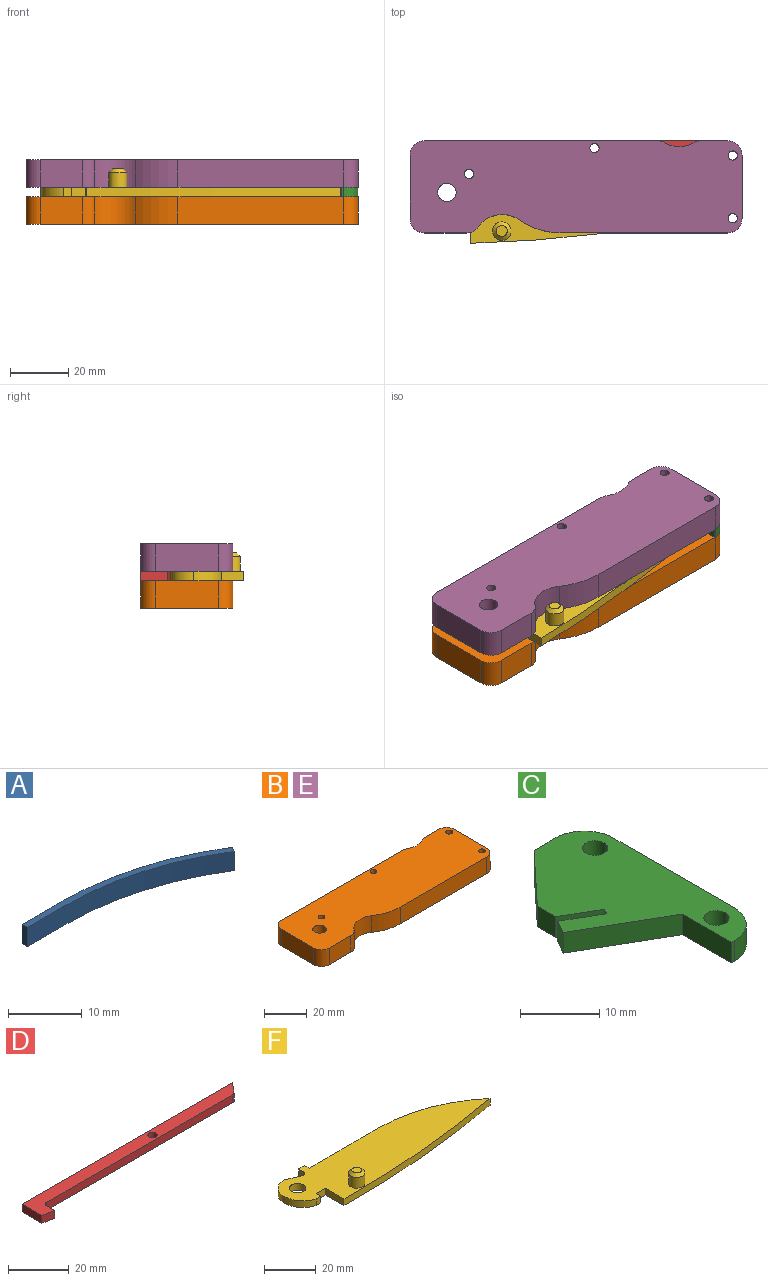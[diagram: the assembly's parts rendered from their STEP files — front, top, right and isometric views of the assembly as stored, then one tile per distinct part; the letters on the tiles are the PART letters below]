
ASSEMBLY  parts=6 mates=5
PART A: 8 faces, bbox 33x8.2x3.2 mm
  f0: plane 7.62x3.18mm, normal (0,1,0), area 24.2mm2, adj f1,f5,f6,f7
  f1: plane 3.18x1.02mm, normal (-1,0,0), area 3.2mm2, adj f0,f2,f6,f7
  f2: plane 7.62x3.18mm, normal (0,-1,0), area 24.2mm2, adj f1,f3,f6,f7
  f3: cylinder r=46.46mm len=24.86mm, axis (0,0,-1), area 83.3mm2, adj f2,f4,f6,f7
  f4: plane 3.18x0.86mm, normal (0.84,-0.54,0), area 3.2mm2, adj f3,f5,f6,f7
  f5: cylinder r=47.48mm len=25.4mm, axis (0,0,-1), area 85.1mm2, adj f0,f4,f6,f7
  f6: plane 33.02x8.22mm, normal (0,0,1), area 34.7mm2, adj f0,f1,f2,f3,f4,f5
  f7: plane 33.02x8.22mm, normal (0,0,-1), area 34.7mm2, adj f0,f1,f2,f3,f4,f5
PART B: 23 faces, bbox 114.3x31.8x9.5 mm
  f0: plane 80.03x9.53mm, normal (0,1,0), area 762.3mm2, adj f11,f12,f15,f20
  f1: plane 14.29x9.53mm, normal (0,-1,0), area 136.1mm2, adj f11,f12,f16,f19
  f2: plane 9.53x8.91mm, normal (0,1,0), area 84.8mm2, adj f11,f12,f18,f21
  f3: plane 21.59x9.53mm, normal (-1,0,0), area 205.6mm2, adj f11,f12,f15,f16
  f4: plane 57.19x9.53mm, normal (0,-1,0), area 544.7mm2, adj f11,f12,f17,f22
  f5: cylinder r=1.59mm len=9.53mm, axis (0,0,-1), area 95mm2, adj f11,f12
  f6: cylinder r=1.59mm len=9.53mm, axis (0,0,-1), area 95mm2, adj f11,f12
  f7: cylinder r=1.59mm len=9.53mm, axis (0,0,-1), area 95mm2, adj f11,f12
  f8: cylinder r=3.17mm len=9.53mm, axis (0,0,-1), area 190mm2, adj f11,f12
  f9: plane 21.59x9.53mm, normal (1,0,0), area 205.6mm2, adj f11,f12,f17,f18
  f10: cylinder r=1.59mm len=9.53mm, axis (0,0,-1), area 95mm2, adj f11,f12
  f11: plane 114.3x31.75mm, normal (0,0,1), area 3427.2mm2, adj f0,f1,f2,f3,f4,f5,f6,f7
  f12: plane 114.3x31.75mm, normal (0,0,-1), area 3427.2mm2, adj f0,f1,f2,f3,f4,f5,f6,f7
  f13: cylinder r=10.16mm len=10.14mm, axis (0,0,1), area 101.1mm2, adj f11,f12,f20,f21
  f14: cylinder r=10.16mm len=14.05mm, axis (0,0,1), area 150.5mm2, adj f11,f12,f19,f22
  f15: cylinder r=5.08mm len=9.53mm, axis (0,0,1), area 76mm2, adj f0,f3,f11,f12
  f16: cylinder r=5.08mm len=9.53mm, axis (0,0,-1), area 76mm2, adj f1,f3,f11,f12
  f17: cylinder r=5.08mm len=9.53mm, axis (0,0,1), area 76mm2, adj f4,f9,f11,f12
  f18: cylinder r=5.08mm len=9.53mm, axis (0,0,-1), area 76mm2, adj f2,f9,f11,f12
  f19: cylinder r=5.08mm len=9.53mm, axis (0,0,1), area 45.9mm2, adj f1,f11,f12,f14
  f20: cylinder r=5.08mm len=9.53mm, axis (0,0,1), area 25.3mm2, adj f0,f11,f12,f13
  f21: cylinder r=5.08mm len=9.53mm, axis (0,0,1), area 25.3mm2, adj f2,f11,f12,f13
  f22: cylinder r=25.4mm len=14.49mm, axis (0,0,1), area 146.8mm2, adj f4,f11,f12,f14
PART C: 17 faces, bbox 19.1x31.8x3.2 mm
  f0: plane 3.18x0.51mm, normal (0,-1,0), area 1.6mm2, adj f1,f6,f9,f15
  f1: plane 31.75x19.05mm, normal (0,0,1), area 340.3mm2, adj f0,f2,f3,f4,f5,f7,f8,f9
  f2: plane 21.59x3.18mm, normal (1,0,0), area 68.5mm2, adj f1,f6,f15,f16
  f3: plane 3.9x3.18mm, normal (0,1,0), area 12.4mm2, adj f1,f6,f8,f16
  f4: cylinder r=1.59mm len=3.18mm, axis (0,0,-1), area 31.7mm2, adj f1,f6
  f5: cylinder r=1.59mm len=3.18mm, axis (0,0,-1), area 31.7mm2, adj f1,f6
  f6: plane 31.75x19.05mm, normal (0,0,-1), area 340.3mm2, adj f0,f2,f3,f4,f5,f7,f8,f9
  f7: plane 3.27x3.18mm, normal (-1,0,0), area 10.4mm2, adj f1,f6,f8,f14
  f8: plane 8.89x8.29mm, normal (-0.73,0.68,0), area 38.6mm2, adj f1,f3,f6,f7
  f9: plane 8.74x3.18mm, normal (-1,0,0), area 27.7mm2, adj f0,f1,f6,f10
  f10: plane 13.46x7.77mm, normal (-0.5,-0.87,0), area 49.4mm2, adj f1,f6,f9,f11
  f11: plane 3.18x2.2mm, normal (-0.87,0.5,0), area 8.1mm2, adj f1,f6,f10,f12
  f12: plane 5.5x3.18mm, normal (0.5,0.87,0), area 20.2mm2, adj f1,f6,f11,f13
  f13: plane 3.18x0.88mm, normal (-0.87,0.5,0), area 3.2mm2, adj f1,f6,f12,f14
  f14: plane 5.5x3.18mm, normal (-0.5,-0.87,0), area 20.2mm2, adj f1,f6,f7,f13
  f15: cylinder r=5.08mm len=5.08mm, axis (0,0,-1), area 25.3mm2, adj f0,f1,f2,f6
  f16: cylinder r=5.08mm len=5.08mm, axis (0,0,-1), area 25.3mm2, adj f1,f2,f3,f6
PART D: 11 faces, bbox 98.2x10.2x3.2 mm
  f0: plane 9.26x3.18mm, normal (-1,0,0), area 29.4mm2, adj f1,f6,f7,f8
  f1: plane 5.08x3.18mm, normal (-0.17,-0.98,0), area 16.4mm2, adj f0,f2,f7,f8
  f2: plane 3.81x3.18mm, normal (1,0,0), area 12.1mm2, adj f1,f7,f8,f9
  f3: plane 87.04x3.18mm, normal (0,-1,0), area 276.3mm2, adj f7,f8,f9,f10
  f4: plane 4.63x3.88mm, normal (0.77,-0.64,0), area 19.2mm2, adj f6,f7,f8,f10
  f5: cylinder r=1.59mm len=3.18mm, axis (0,0,-1), area 31.7mm2, adj f7,f8
  f6: plane 98.24x3.18mm, normal (0,1,0), area 311.9mm2, adj f0,f4,f7,f8
  f7: plane 98.24x10.16mm, normal (0,0,1), area 504.2mm2, adj f0,f1,f2,f3,f4,f5,f6,f9
  f8: plane 98.24x10.16mm, normal (0,0,-1), area 504.2mm2, adj f0,f1,f2,f3,f4,f5,f6,f9
  f9: cylinder r=1.27mm len=3.18mm, axis (0,0,1), area 6.3mm2, adj f2,f3,f7,f8
  f10: cylinder r=1.27mm len=3.18mm, axis (0,0,-1), area 3.5mm2, adj f3,f4,f7,f8
PART E: same geometry as B
PART F: 20 faces, bbox 102.9x26.7x9.5 mm
  f0: plane 3.18x2.54mm, normal (1,0,0), area 8.1mm2, adj f1,f12,f14,f15
  f1: plane 3.28x3.18mm, normal (0,1,0), area 10.4mm2, adj f0,f2,f14,f15
  f2: plane 3.18x2.81mm, normal (-1,0,0), area 8.9mm2, adj f1,f14,f15,f19
  f3: plane 7.23x3.18mm, normal (0.38,0.92,0), area 24.9mm2, adj f4,f14,f15,f19
  f4: cylinder r=7.62mm len=7.62mm, axis (0,0,-1), area 38mm2, adj f3,f5,f14,f15
  f5: cylinder r=10.58mm len=10.16mm, axis (0,0,-1), area 43.2mm2, adj f4,f6,f14,f15
  f6: plane 3.18x2.54mm, normal (0,-1,0), area 8.1mm2, adj f5,f7,f14,f15
  f7: plane 3.18x2.54mm, normal (1,0,0), area 8.1mm2, adj f6,f8,f14,f15
  f8: plane 5.08x3.18mm, normal (0,-1,0), area 16.1mm2, adj f7,f9,f14,f15
  f9: plane 10.16x3.18mm, normal (-1,0,0), area 32.3mm2, adj f8,f10,f14,f15
  f10: cylinder r=457.2mm len=87.63mm, axis (0,0,-1), area 279.7mm2, adj f9,f11,f14,f15
  f11: cylinder r=68.09mm len=44.45mm, axis (0,0,-1), area 153.8mm2, adj f10,f12,f14,f15
  f12: plane 38.1x3.18mm, normal (0,1,0), area 121mm2, adj f0,f11,f14,f15
  f13: cylinder r=3.17mm len=6.35mm, axis (0,0,-1), area 63.3mm2, adj f14,f15
  f14: plane 102.87x26.69mm, normal (0,0,1), area 1829mm2, adj f0,f1,f2,f3,f4,f5,f6,f7
  f15: plane 102.87x26.69mm, normal (0,0,-1), area 1860.6mm2, adj f0,f1,f2,f3,f4,f5,f6,f7
  f16: cylinder r=3.17mm len=6.35mm, axis (0,0,-1), area 101.3mm2, adj f14,f18
  f17: plane 3.81x3.81mm, normal (0,0,1), area 11.4mm2, adj f18
  f18: cone r=1.91mm half-angle=45deg, axis (0,0,-1), area 28.7mm2, adj f16,f17
  f19: cylinder r=1.59mm len=3.18mm, axis (0,0,1), area 9.9mm2, adj f2,f3,f14,f15
PLACE A rot(axis=(-0.26,-0.97,0),180deg) t=(102.02,15.53,12.7)mm
PLACE B t=(53.79,11.76,0)mm fixed
PLACE C t=(88.9,0,9.52)mm
PLACE D rot(axis=(0,0,-1),0deg) t=(63.5,29.21,9.52)mm
PLACE E t=(53.79,11.76,12.7)mm
PLACE F rot(axis=(0,0,1),2deg) t=(12.7,13.97,9.52)mm
MATE revolute B.f6 <-> D.f5  axis (0,0,1) through (63.5,29.21,9.52)mm
MATE revolute B.f8 <-> F.f13  axis (0,0,1) through (12.7,13.97,9.52)mm
MATE fastened B.f5 <-> C.f4  axis (0,0,1) through (111.13,26.67,9.52)mm
MATE fastened C.f12 <-> A.f2  axis (0.5,0.87,0) through (102.02,15.53,12.7)mm
MATE fastened B.f8 <-> E.f8  axis (0,0,1) through (12.7,13.97,9.52)mm
